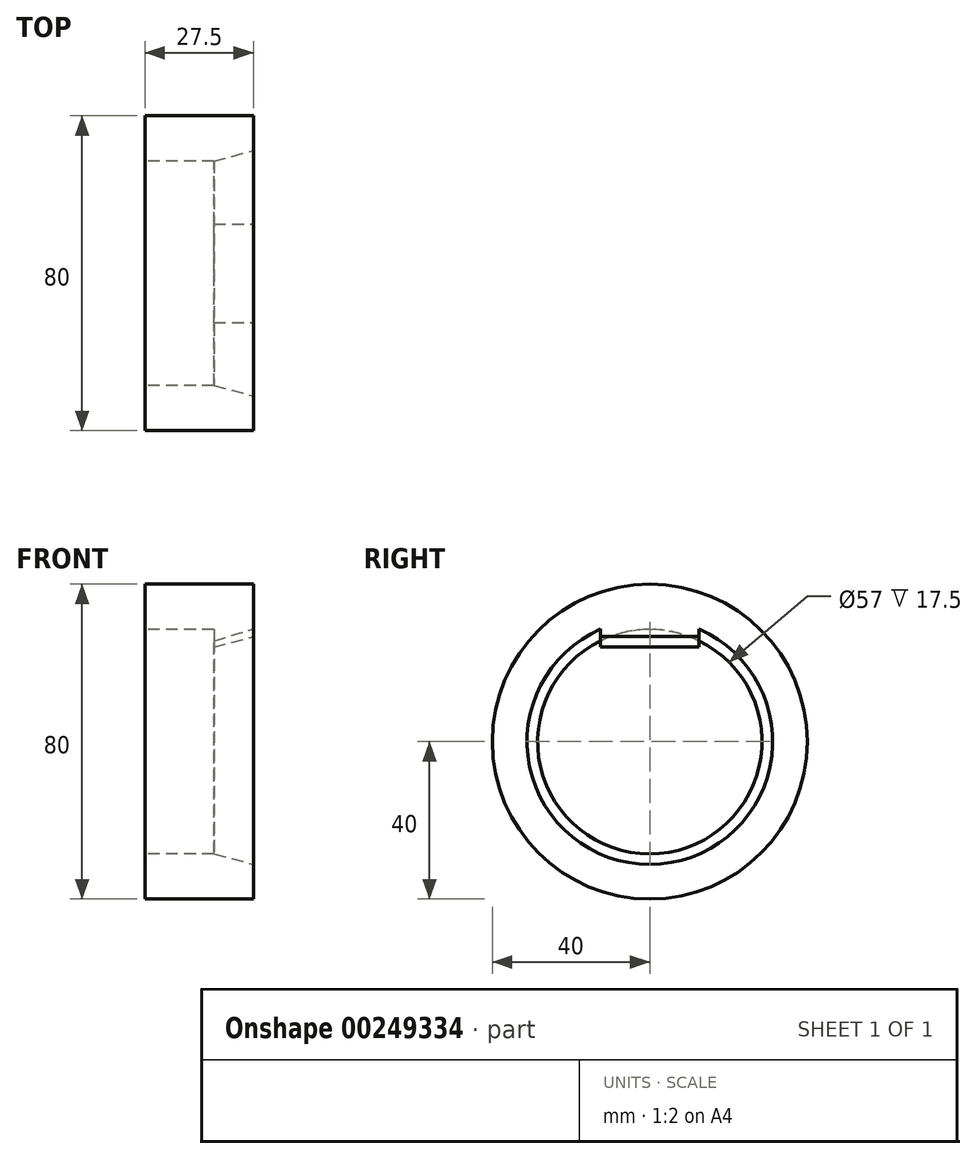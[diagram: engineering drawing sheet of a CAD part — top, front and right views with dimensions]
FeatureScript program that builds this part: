
annotation { "Feature Type Name" : "Feature", "Feature Type Description" : "" }
export const myFeature = defineFeature(function(context is Context, id is Id, definition is map)
    precondition{}
    {
        {
            var Q0;
            Q0=qCreatedBy(makeId("Front.planeOp"),FACE);
            var sketch = newSketch(context, id + "F0", { "sketchPlane" : qUnion([Q0])});
            skLineSegment(sketch, "E0", {"start": v(-12.55, 0) * mm, "end": v(0, 0) * mm, "construction": true});
            skLineSegment(sketch, "E1", {"start": v(0, 6.5) * mm, "end": v(0, 23.83) * mm, "construction": true});
            skLineSegment(sketch, "E2", {"start": v(0, 23.83) * mm, "end": v(5.6, 25.4) * mm, "construction": true});
            skLineSegment(sketch, "E3", {"start": v(5.6, 25.4) * mm, "end": v(5.6, 28.5) * mm, "construction": true});
            skLineSegment(sketch, "E4", {"start": v(5.6, 28.5) * mm, "end": v(-11.9, 28.5) * mm});
            skLineSegment(sketch, "E5", {"start": v(-11.9, 28.5) * mm, "end": v(-11.9, 6.5) * mm, "construction": true});
            skLineSegment(sketch, "E6", {"start": v(-2, 6.5) * mm, "end": v(-11.9, 6.5) * mm, "construction": true});
            skLineSegment(sketch, "E7", {"start": v(0, 23.83) * mm, "end": v(12.27, 23.83) * mm, "construction": true});
            skLineSegment(sketch, "E8", {"start": v(5.6, 25.4) * mm, "end": v(-2, 23.27) * mm, "construction": true});
            skLineSegment(sketch, "E9", {"start": v(-2, 23.27) * mm, "end": v(-2, 6.5) * mm, "construction": true});
            skLineSegment(sketch, "E10", {"start": v(-11.9, 28.5) * mm, "end": v(-11.9, 40) * mm});
            skLineSegment(sketch, "E11", {"start": v(-11.9, 40) * mm, "end": v(15.6, 40) * mm});
            skLineSegment(sketch, "E12", {"start": v(15.6, 40) * mm, "end": v(15.6, 31.2) * mm});
            skLineSegment(sketch, "E13", {"start": v(5.6, 28.5) * mm, "end": v(15.6, 31.2) * mm});
            skSolve(sketch);
        }
        {
            var Q0;
            Q0=makeQuery(id+"F0.imprint","IMPRINT",FACE,{"disambiguationData":[TD([[makeQuery(id+"F0.imprint","IMPRINT",EDGE,{"derivedFrom":sQuery(id+"F0.wireOp",EDGE,"E4")}),-1.0]])]});
            var Q1;
            Q1=sQuery(id+"F0.wireOp",EDGE,"E0");
            revolve(context, id + "F1", {"entities" : qUnion([Q0]), "axis" : qUnion([Q1]), "revolveType" : RevolveType.FULL});
        }
        {
            var Q0;
            Q0=qCreatedBy(makeId("Front.planeOp"),FACE);
            var sketch = newSketch(context, id + "F2", { "sketchPlane" : qUnion([Q0])});
            skLineSegment(sketch, "E14", {"start": v(-24.73, 0) * mm, "end": v(24.73, 0) * mm, "construction": true});
            skLineSegment(sketch, "E15", {"start": v(-11.9, 28.5) * mm, "end": v(5.6, 28.5) * mm, "construction": true});
            skLineSegment(sketch, "E16", {"start": v(5.6, 28.5) * mm, "end": v(15.6, 31.2) * mm});
            skLineSegment(sketch, "E17", {"start": v(5.6, 28.5) * mm, "end": v(5.6, 24) * mm});
            skLineSegment(sketch, "E18", {"start": v(5.6, 24) * mm, "end": v(15.6, 26.7) * mm});
            skLineSegment(sketch, "E19", {"start": v(15.6, 31.2) * mm, "end": v(15.6, 26.7) * mm});
            skSolve(sketch);
        }
        {
            var Q0;
            Q0 = qSketchRegion(id + "F2", true);
            extrude(context, id + "F3", {"entities" : qUnion([Q0]), "operationType" : NewBodyOperationType.ADD, "depth" : 25 * mm, "symmetric" : true});
        }
    });
